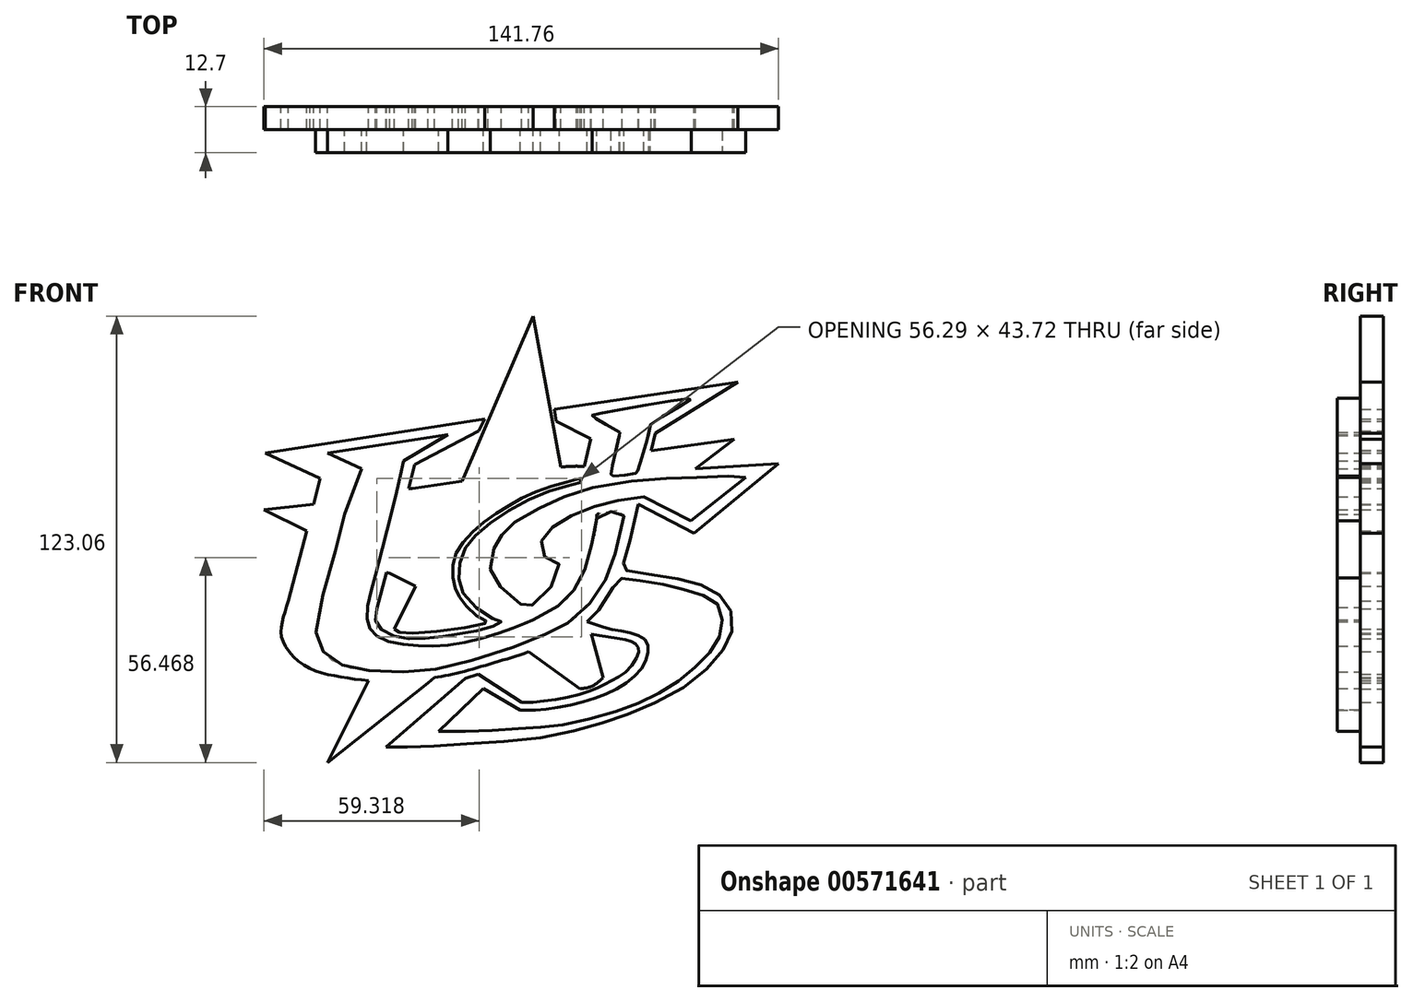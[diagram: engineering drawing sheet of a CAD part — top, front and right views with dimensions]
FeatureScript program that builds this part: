
annotation { "Feature Type Name" : "Feature", "Feature Type Description" : "" }
export const myFeature = defineFeature(function(context is Context, id is Id, definition is map)
    precondition{}
    {
        {
            var Q0;
            Q0=qCreatedBy(makeId("Front.planeOp"),FACE);
            var sketch = newSketch(context, id + "F0", { "sketchPlane" : qUnion([Q0])});
            skLineSegment(sketch, "E0", {"start": v(-53.01, -48.61) * mm, "end": v(-42.44, -27.38) * mm});
            skLineSegment(sketch, "E1", {"start": v(-25.38, -26.7) * mm, "end": v(-53.01, -48.61) * mm});
            skLineSegment(sketch, "E2", {"start": v(-34.65, -11.81) * mm, "end": v(-28.77, 0) * mm});
            skLineSegment(sketch, "E3", {"start": v(-28.77, 0) * mm, "end": v(-35.85, 3.52) * mm});
            skFitSpline(sketch, "E4", {"points": [v(-34.65, -11.81) * mm, v(-33.82, -12.56) * mm, v(-26.31, -12.76) * mm, v(-8.97, -10.03) * mm, v(-9.02, -9.77) * mm, v(-11.35, -8.56) * mm, v(-15.77, -4.35) * mm, v(-17.62, -1.2) * mm, v(-18.48, 2.3) * mm, v(-18.17, 7.52) * mm, v(-15.49, 12.23) * mm, v(-10.48, 17.27) * mm, v(-3.91, 21.7) * mm, v(2.6, 25.24) * mm, v(11.26, 28.22) * mm, v(15.52, 29.42) * mm, v(15.76, 29.96) * mm, v(16.13, 32.8) * mm, v(14.98, 33.03) * mm, v(11.24, 32.91) * mm], "startDerivative": vector(24.08, -30.92) * mm, "endDerivative": vector(-84.78, -1.1) * mm});
            skFitSpline(sketch, "E5", {"points": [v(11.24, 32.91) * mm, v(3.63, 74.45) * mm], "startDerivative": vector(-7.61, 41.54) * mm, "endDerivative": vector(-7.61, 41.54) * mm});
            skLineSegment(sketch, "E6", {"start": v(3.63, 74.45) * mm, "end": v(-16.03, 28.99) * mm});
            skLineSegment(sketch, "E7", {"start": v(-16.03, 28.99) * mm, "end": v(-29.66, 26.94) * mm});
            skLineSegment(sketch, "E8", {"start": v(-70.6, 21) * mm, "end": v(-57.8, 22.45) * mm});
            skLineSegment(sketch, "E9", {"start": v(-59.38, 15.46) * mm, "end": v(-70.6, 21) * mm});
            skLineSegment(sketch, "E10", {"start": v(3.63, -19.06) * mm, "end": v(16.5, -28.29) * mm});
            skLineSegment(sketch, "E11", {"start": v(20.05, -15) * mm, "end": v(22.9, -25.25) * mm});
            skLineSegment(sketch, "E12", {"start": v(19.78, -14.03) * mm, "end": v(20.05, -15) * mm});
            skFitSpline(sketch, "E13", {"points": [v(16.5, -28.29) * mm, v(19.86, -27.55) * mm, v(22.9, -25.25) * mm], "startDerivative": vector(7.13, 0.8) * mm, "endDerivative": vector(5.66, 5.25) * mm});
            skLineSegment(sketch, "E14", {"start": v(37.05, 37.4) * mm, "end": v(58.95, 40.44) * mm});
            skLineSegment(sketch, "E15", {"start": v(58.95, 40.44) * mm, "end": v(49.62, 33.34) * mm});
            skLineSegment(sketch, "E16", {"start": v(-53.05, 36.68) * mm, "end": v(-19.88, 41.74) * mm});
            skLineSegment(sketch, "E17", {"start": v(-19.88, 41.74) * mm, "end": v(-32.06, 34.5) * mm});
            skLineSegment(sketch, "E18", {"start": v(-53.05, 36.68) * mm, "end": v(-43.64, 32.34) * mm});
            skPoint(sketch, "E19.1.internal.snap0", {"position": v(-48.34, 34.5) * mm});
            skFitSpline(sketch, "E19", {"points": [v(-43.64, 32.34) * mm, v(-48.34, 19.8) * mm], "startDerivative": vector(-4.7, -12.54) * mm, "endDerivative": vector(-4.7, -12.54) * mm});
            skFitSpline(sketch, "E20", {"points": [v(-48.34, 19.8) * mm, v(-52.08, 5.2) * mm, v(-56.3, -11.8) * mm, v(-55.17, -16.37) * mm, v(-52.87, -19.62) * mm, v(-47.24, -22.35) * mm, v(-39.64, -23.46) * mm, v(-27.88, -23.46) * mm, v(-17.77, -21.7) * mm, v(-0.7, -16.46) * mm, v(8.5, -12.57) * mm, v(13.56, -9.94) * mm, v(19.91, -3.93) * mm, v(23.83, 2.38) * mm, v(26.48, 10.27) * mm, v(28.58, 20.91) * mm, v(27.42, 20.91) * mm, v(21.23, 19.8) * mm, v(21.08, 19.29) * mm, v(20.37, 14.47) * mm, v(18.5, 7.02) * mm, v(16.8, 2.11) * mm, v(13.7, -2.38) * mm, v(10.4, -5.52) * mm, v(3.63, -9.27) * mm], "startDerivative": vector(-53.07, -226.8) * mm, "endDerivative": vector(-174.22, -86.8) * mm});
            skFitSpline(sketch, "E21", {"points": [v(3.63, -9.27) * mm, v(-0.27, -10.86) * mm, v(-9.19, -13.97) * mm, v(-20.78, -16.4) * mm, v(-29.54, -16.3) * mm, v(-37.99, -14.63) * mm, v(-41.38, -11.63) * mm, v(-42.16, -7.2) * mm, v(-40.05, 2.46) * mm, v(-38.12, 9.66) * mm, v(-34.4, 24.26) * mm, v(-32.06, 34.5) * mm], "startDerivative": vector(-54.34, -22.81) * mm, "endDerivative": vector(20.16, 92.36) * mm});
            skFitSpline(sketch, "E22", {"points": [v(27.4, 42.38) * mm, v(19.91, 46.96) * mm, v(20.47, 47.26) * mm, v(46.94, 51.73) * mm, v(47.06, 51.54) * mm, v(35.66, 44.37) * mm, v(35.72, 43.95) * mm, v(32.29, 31.4) * mm, v(32.04, 31.1) * mm, v(25.23, 30.38) * mm, v(24.99, 30.74) * mm, v(27.28, 41.54) * mm], "startDerivative": vector(-88.3, 50.17) * mm, "endDerivative": vector(23.9, 106.61) * mm});
            skLineSegment(sketch, "E23", {"start": v(27.4, 42.38) * mm, "end": v(27.28, 41.54) * mm});
            skLineSegment(sketch, "E24", {"start": v(47.08, 18) * mm, "end": v(62.17, 29.94) * mm});
            skLineSegment(sketch, "E25", {"start": v(47.08, 18) * mm, "end": v(34.03, 24.56) * mm});
            skFitSpline(sketch, "E26", {"points": [v(62.17, 29.94) * mm, v(59.05, 30.34) * mm, v(47.71, 29.94) * mm, v(35.05, 29.4) * mm, v(16.8, 26.32) * mm, v(8.2, 22.8) * mm, v(-1.08, 17.88) * mm, v(-4.63, 14.38) * mm, v(-5.77, 13.21) * mm, v(-7.75, 8.75) * mm, v(-7.95, 3.63) * mm, v(-4.3, -1.24) * mm, v(1.4, -5.75) * mm, v(2.16, -5.7) * mm, v(6.87, -2.7) * mm, v(10.78, 5.96) * mm, v(10.37, 6.12) * mm, v(6.47, 8.45) * mm, v(5.7, 11.74) * mm, v(7.38, 14.89) * mm, v(11.49, 17.98) * mm, v(18.5, 21.22) * mm, v(25.72, 23.37) * mm, v(34.03, 24.56) * mm], "startDerivative": vector(-81.19, 16.61) * mm, "endDerivative": vector(164.27, 18.85) * mm});
            skFitSpline(sketch, "E27", {"points": [v(18.5, -9.76) * mm, v(22.13, -5.96) * mm, v(27.42, 2.14) * mm, v(28.08, 2.14) * mm, v(35.61, 1.14) * mm, v(43.93, -0.65) * mm, v(51.32, -2.95) * mm, v(54.97, -5.74) * mm, v(55.62, -10.86) * mm, v(53.83, -16.14) * mm, v(49.02, -21.66) * mm, v(42.51, -26.9) * mm, v(34.03, -31.56) * mm, v(23.95, -35.26) * mm, v(10.78, -38.44) * mm, v(2.4, -39.1) * mm, v(-9.54, -39.89) * mm, v(-22.44, -40.07) * mm], "startDerivative": vector(68.4, 55.62) * mm, "endDerivative": vector(-168.08, 0.41) * mm});
            skLineSegment(sketch, "E28", {"start": v(-22.44, -40.07) * mm, "end": v(-10.14, -28.25) * mm});
            skLineSegment(sketch, "E29", {"start": v(-10.14, -28.25) * mm, "end": v(0, -34.16) * mm});
            skFitSpline(sketch, "E30", {"points": [v(0, -34.16) * mm, v(4.63, -34.16) * mm, v(15.3, -32.47) * mm, v(25.85, -28.67) * mm, v(32.9, -23.37) * mm, v(35.26, -18.12) * mm, v(34.36, -14.74) * mm, v(29.83, -12.81) * mm, v(23.8, -11.55) * mm, v(18.5, -9.76) * mm], "startDerivative": vector(44.3, -1.92) * mm, "endDerivative": vector(-50.66, 19.13) * mm});
            skLineSegment(sketch, "E31", {"start": v(-70.25, 36.68) * mm, "end": v(-55.05, 29.73) * mm});
            skLineSegment(sketch, "E32", {"start": v(-55.05, 29.73) * mm, "end": v(-63.8, -4.14) * mm});
            skLineSegment(sketch, "E33", {"start": v(-70.25, 36.68) * mm, "end": v(-9.8, 46.12) * mm});
            skLineSegment(sketch, "E34", {"start": v(-9.8, 46.12) * mm, "end": v(-11.45, 42.82) * mm});
            skLineSegment(sketch, "E35", {"start": v(-11.45, 42.82) * mm, "end": v(-29.02, 33.5) * mm});
            skLineSegment(sketch, "E36", {"start": v(-29.02, 33.5) * mm, "end": v(-39.42, -6.3) * mm});
            skLineSegment(sketch, "E37", {"start": v(9.41, 48.8) * mm, "end": v(60.02, 56.2) * mm});
            skLineSegment(sketch, "E38", {"start": v(60.02, 56.2) * mm, "end": v(37.3, 42.11) * mm});
            skLineSegment(sketch, "E39", {"start": v(37.3, 42.11) * mm, "end": v(34.56, 31.57) * mm});
            skLineSegment(sketch, "E40", {"start": v(34.56, 31.57) * mm, "end": v(71.17, 33.7) * mm});
            skLineSegment(sketch, "E41", {"start": v(71.17, 33.7) * mm, "end": v(47.96, 14.53) * mm});
            skLineSegment(sketch, "E42", {"start": v(47.96, 14.53) * mm, "end": v(32.53, 22.63) * mm});
            skLineSegment(sketch, "E43", {"start": v(9.41, 48.8) * mm, "end": v(9.91, 45.38) * mm});
            skLineSegment(sketch, "E44", {"start": v(9.91, 45.38) * mm, "end": v(19.48, 40.62) * mm});
            skLineSegment(sketch, "E45", {"start": v(19.48, 40.62) * mm, "end": v(16.58, 28.51) * mm});
            skLineSegment(sketch, "E46", {"start": v(-36.91, -44.33) * mm, "end": v(-15.02, -25.4) * mm});
            skLineSegment(sketch, "E47", {"start": v(-15.02, -25.4) * mm, "end": v(-11.47, -24.25) * mm});
            skLineSegment(sketch, "E48", {"start": v(-11.47, -24.25) * mm, "end": v(0.47, -31.97) * mm});
            skFitSpline(sketch, "E49", {"points": [v(-36.91, -44.33) * mm, v(-29.47, -44.33) * mm, v(-14.64, -43.5) * mm, v(6.9, -41.58) * mm, v(22.02, -37.9) * mm, v(33.4, -33.87) * mm, v(47.27, -26.45) * mm, v(55.4, -18.25) * mm, v(58.36, -12.04) * mm, v(57.57, -5.74) * mm, v(53.2, -1.23) * mm, v(45.86, 1.5) * mm, v(35, 3.39) * mm, v(28.16, 4.65) * mm, v(28.08, 5.04) * mm, v(29.89, 11.31) * mm, v(31.58, 18.49) * mm, v(32.53, 22.63) * mm], "startDerivative": vector(127.5, -2.25) * mm, "endDerivative": vector(22.44, 95.58) * mm});
            skFitSpline(sketch, "E50", {"points": [v(16.58, 28.51) * mm, v(10.78, 27.05) * mm, v(0, 22.63) * mm, v(-10.46, 15.62) * mm, v(-15.3, 10.27) * mm, v(-16.91, 3.6) * mm, v(-15.7, -1.84) * mm, v(-8.3, -8.59) * mm, v(-5.25, -9.7) * mm, v(-5.5, -10.26) * mm, v(-10.88, -12.03) * mm, v(-18.17, -13.4) * mm, v(-26.09, -14.37) * mm, v(-32.55, -14.28) * mm, v(-37.82, -12.3) * mm, v(-39.76, -9.65) * mm, v(-39.42, -6.3) * mm], "startDerivative": vector(-86.4, -19.06) * mm, "endDerivative": vector(17.82, 74.59) * mm});
            skFitSpline(sketch, "E51", {"points": [v(-63.8, -4.14) * mm, v(-65.64, -10.48) * mm, v(-65.19, -15.5) * mm, v(-59.26, -22) * mm, v(-50.53, -24.83) * mm, v(-40.04, -26.15) * mm, v(-28.88, -25.85) * mm, v(-18.8, -24.33) * mm, v(-5.15, -20.52) * mm, v(8.51, -15.37) * mm, v(14.07, -12) * mm, v(14.32, -12.14) * mm, v(17.37, -12.84) * mm, v(22.92, -13.8) * mm, v(28.8, -14.74) * mm, v(31.38, -15.63) * mm, v(32.53, -16.89) * mm, v(32.53, -18.58) * mm, v(29.6, -23.22) * mm, v(24.99, -26.2) * mm, v(20.37, -28.5) * mm, v(11.47, -30.94) * mm, v(2.22, -32.08) * mm, v(0.47, -31.97) * mm], "startDerivative": vector(-49.43, -143.96) * mm, "endDerivative": vector(-58.97, 8.12) * mm});
            skLineSegment(sketch, "E52", {"start": v(-42.44, -27.38) * mm, "end": v(-41.77, -26.04) * mm});
            skLineSegment(sketch, "E53", {"start": v(-25.38, -26.7) * mm, "end": v(-23.64, -25.23) * mm});
            skLineSegment(sketch, "E54", {"start": v(-59.38, 15.46) * mm, "end": v(-58.8, 15.17) * mm});
            skLineSegment(sketch, "E55", {"start": v(-57.8, 22.45) * mm, "end": v(-56.88, 22.64) * mm});
            skLineSegment(sketch, "E56", {"start": v(-35.85, 3.52) * mm, "end": v(-36.79, 3.77) * mm});
            skLineSegment(sketch, "E57", {"start": v(-29.66, 26.94) * mm, "end": v(-30.73, 26.94) * mm});
            skLineSegment(sketch, "E58", {"start": v(37.05, 37.4) * mm, "end": v(36.06, 37.33) * mm});
            skLineSegment(sketch, "E59", {"start": v(49.62, 33.34) * mm, "end": v(48.35, 32.37) * mm});
            skLineSegment(sketch, "E60", {"start": v(17.67, 33.03) * mm, "end": v(14.98, 33.03) * mm});
            skLineSegment(sketch, "E61", {"start": v(15.52, 29.42) * mm, "end": v(16.87, 29.72) * mm});
            skLineSegment(sketch, "E62", {"start": v(3.63, -19.06) * mm, "end": v(2.3, -18.12) * mm});
            skLineSegment(sketch, "E63", {"start": v(19.78, -14.03) * mm, "end": v(19.57, -13.24) * mm});
            skSolve(sketch);
        }
        {
            var Q0;
            Q0=makeQuery(id+"F0.imprint","IMPRINT",FACE,{"disambiguationData":[TD([[makeQuery(id+"F0.imprint","IMPRINT",EDGE,{"derivedFrom":sQuery(id+"F0.wireOp",EDGE,"E0")}),-1.0]])]});
            var Q1;
            Q1=makeQuery(id+"F0.imprint","IMPRINT",FACE,{"disambiguationData":[TD([[makeQuery(id+"F0.imprint","IMPRINT",EDGE,{"derivedFrom":sQuery(id+"F0.wireOp",EDGE,"E2")}),-1.0]])]});
            var Q2;
            Q2=makeQuery(id+"F0.imprint","IMPRINT",FACE,{"disambiguationData":[TD([[makeQuery(id+"F0.imprint","IMPRINT",EDGE,{"derivedFrom":sQuery(id+"F0.wireOp",EDGE,"E10")}),1.0]])]});
            var Q3;
            Q3=makeQuery(id+"F0.imprint","IMPRINT",FACE,{"disambiguationData":[TD([[makeQuery(id+"F0.imprint","IMPRINT",EDGE,{"derivedFrom":sQuery(id+"F0.wireOp",EDGE,"E14")}),-1.0]])]});
            var Q4;
            Q4=makeQuery(id+"F0.imprint","IMPRINT",FACE,{"disambiguationData":[TD([[makeQuery(id+"F0.imprint","IMPRINT",EDGE,{"derivedFrom":sQuery(id+"F0.wireOp",EDGE,"E16")}),1.0]])]});
            var Q5;
            Q5=makeQuery(id+"F0.imprint","IMPRINT",FACE,{"disambiguationData":[TD([[makeQuery(id+"F0.imprint","IMPRINT",EDGE,{"derivedFrom":sQuery(id+"F0.wireOp",EDGE,"E8")}),-1.0]])]});
            extrude(context, id + "F1", {"entities" : qUnion([Q0, Q1, Q2, Q3, Q4, Q5]), "depth" : 6.35 * mm, "offsetDistance" : 25.4 * mm});
        }
        {
            var Q0;
            Q0 = qSketchRegion(id + "F0", true);
            extrude(context, id + "F2", {"entities" : qUnion([Q0]), "operationType" : NewBodyOperationType.ADD, "depth" : 6.35 * mm, "offsetDistance" : 25.4 * mm});
        }
        {
            var Q0;
            Q0=makeQuery(id+"F0.imprint","IMPRINT",FACE,{"disambiguationData":[TD([[makeQuery(id+"F0.imprint","IMPRINT",EDGE,{"derivedFrom":sQuery(id+"F0.wireOp",EDGE,"E16")}),-1.0]])]});
            var Q1;
            Q1=makeQuery(id+"F0.imprint","IMPRINT",FACE,{"disambiguationData":[TD([[makeQuery(id+"F0.imprint","IMPRINT",EDGE,{"derivedFrom":sQuery(id+"F0.wireOp",EDGE,"E22")}),-1.0]])]});
            var Q2;
            Q2=makeQuery(id+"F0.imprint","IMPRINT",FACE,{"disambiguationData":[TD([[makeQuery(id+"F0.imprint","IMPRINT",EDGE,{"derivedFrom":sQuery(id+"F0.wireOp",EDGE,"E27")}),-1.0]])]});
            var Q3;
            Q3=makeQuery(id+"F0.imprint","IMPRINT",FACE,{"disambiguationData":[TD([[makeQuery(id+"F0.imprint","IMPRINT",EDGE,{"derivedFrom":sQuery(id+"F0.wireOp",EDGE,"E24")}),1.0]])]});
            extrude(context, id + "F3", {"entities" : qUnion([Q0, Q1, Q2, Q3]), "operationType" : NewBodyOperationType.ADD, "depth" : 12.7 * mm, "offsetDistance" : 25.4 * mm});
        }
    });
